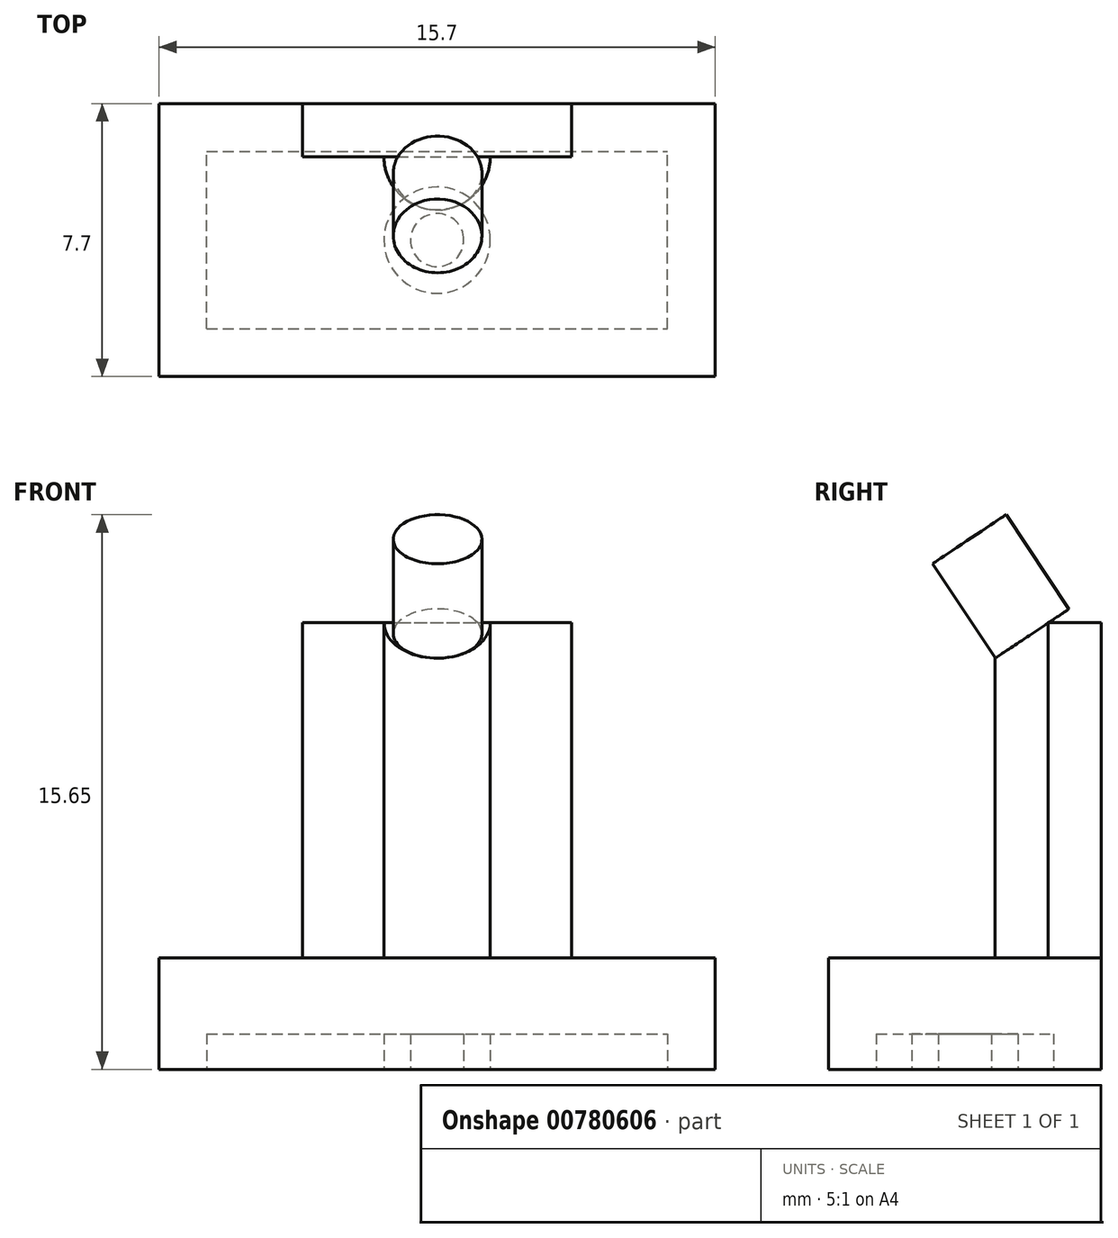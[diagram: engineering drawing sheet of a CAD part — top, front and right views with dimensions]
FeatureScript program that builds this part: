
annotation { "Feature Type Name" : "Feature", "Feature Type Description" : "" }
export const myFeature = defineFeature(function(context is Context, id is Id, definition is map)
    precondition{}
    {
        {
            var Q0;
            Q0=qCreatedBy(makeId("Front.planeOp"),FACE);
            var sketch = newSketch(context, id + "F0", { "sketchPlane" : qUnion([Q0])});
            skLineSegment(sketch, "E0.bottom", {"start": v(0, 0) * mm, "end": v(15.7, 0) * mm});
            skLineSegment(sketch, "E0.top", {"start": v(0, 3.15) * mm, "end": v(15.7, 3.15) * mm});
            skLineSegment(sketch, "E0.left", {"start": v(0, 0) * mm, "end": v(0, 3.15) * mm});
            skLineSegment(sketch, "E0.right", {"start": v(15.7, 0) * mm, "end": v(15.7, 3.15) * mm});
            skLineSegment(sketch, "E1", {"start": v(4.05, 3.15) * mm, "end": v(4.05, 12.6) * mm});
            skLineSegment(sketch, "E2", {"start": v(4.05, 12.6) * mm, "end": v(11.65, 12.6) * mm});
            skLineSegment(sketch, "E3", {"start": v(11.65, 12.6) * mm, "end": v(11.65, 3.15) * mm});
            skSolve(sketch);
        }
        {
            var Q0;
            Q0=makeQuery(id+"F0.imprint","IMPRINT",FACE,{"disambiguationData":[TD([[makeQuery(id+"F0.imprint","IMPRINT",EDGE,{"derivedFrom":sQuery(id+"F0.wireOp",EDGE,"E0.bottom")}),1.0]])]});
            extrude(context, id + "F1", {"entities" : qUnion([Q0]), "depth" : 7.7 * mm, "offsetDistance" : 25 * mm});
        }
        {
            var Q0;
            {var subQ0=sQuery(id+"F0.wireOp",EDGE,"E1");Q0=makeQuery(id+"F0.imprint","IMPRINT",FACE,{"disambiguationData":[TD([[makeQuery(id+"F0.imprint","IMPRINT",EDGE,{"derivedFrom":subQ0}),-1.0]])]});}
            extrude(context, id + "F2", {"entities" : qUnion([Q0]), "operationType" : NewBodyOperationType.ADD, "depth" : 1.5 * mm, "offsetDistance" : 25 * mm});
        }
        {
            var Q0;
            Q0=makeQuery(id+"F1.opExtrude","SWEPT_FACE",FACE,{"disambiguationData":[OSD([sQuery(id+"F0.wireOp",EDGE,"E0.top")])]});
            var sketch = newSketch(context, id + "F3", { "sketchPlane" : qUnion([Q0])});
            skCircle(sketch, "E4", {"center": v(7.85, -1.5) * mm, "radius": 1.5 * mm});
            skSolve(sketch);
        }
        {
            var Q0;
            Q0=qSketchRegion(id+"F3",true);
            extrude(context, id + "F4", {"entities" : qUnion([Q0]), "operationType" : NewBodyOperationType.ADD, "depth" : 9.45 * mm, "offsetDistance" : 25 * mm});
        }
        {
            var Q0;
            Q0=makeQuery(id+"F1.opExtrude","SWEPT_FACE",FACE,{"disambiguationData":[OSD([sQuery(id+"F0.wireOp",EDGE,"E0.bottom")])]});
            var sketch = newSketch(context, id + "F5", { "sketchPlane" : qUnion([Q0])});
            skLineSegment(sketch, "E5.0", {"start": v(1.35, 6.35) * mm, "end": v(14.35, 6.35) * mm});
            skLineSegment(sketch, "E5.1", {"start": v(1.35, 6.35) * mm, "end": v(1.35, 1.35) * mm});
            skLineSegment(sketch, "E5.2", {"start": v(1.35, 1.35) * mm, "end": v(14.35, 1.35) * mm});
            skLineSegment(sketch, "E5.3", {"start": v(14.35, 6.35) * mm, "end": v(14.35, 1.35) * mm});
            skCircle(sketch, "E6", {"center": v(7.85, 3.85) * mm, "radius": 1.5 * mm});
            skPoint(sketch, "E6.centerSnap0", {"position": v(1.35, 3.85) * mm});
            skPoint(sketch, "E6.centerSnap1", {"position": v(7.85, 6.35) * mm});
            skCircle(sketch, "E7", {"center": v(7.85, 3.85) * mm, "radius": 0.75 * mm});
            skSolve(sketch);
        }
        {
            var Q0;
            Q0=makeQuery(id+"F5.imprint","IMPRINT",FACE,{"disambiguationData":[TD([[makeQuery(id+"F5.imprint","IMPRINT",EDGE,{"derivedFrom":sQuery(id+"F5.wireOp",EDGE,"E5.0")}),-1.0]])]});
            var Q1;
            Q1=makeQuery(id+"F5.imprint","IMPRINT",FACE,{"disambiguationData":[TD([[makeQuery(id+"F5.imprint","IMPRINT",EDGE,{"derivedFrom":sQuery(id+"F5.wireOp",EDGE,"E7")}),1.0]])]});
            extrude(context, id + "F6", {"entities" : qUnion([Q0, Q1]), "operationType" : NewBodyOperationType.REMOVE, "oppositeDirection" : true, "depth" : 1 * mm, "offsetDistance" : 25 * mm});
        }
        {
            var Q0;
            Q0=makeQuery(id+"F2.opExtrude","SWEPT_FACE",FACE,{"disambiguationData":[OSD([sQuery(id+"F0.wireOp",EDGE,"E3")])]});
            var sketch = newSketch(context, id + "F7", { "sketchPlane" : qUnion([Q0])});
            skLineSegment(sketch, "E8", {"start": v(-1.5, 12.6) * mm, "end": v(-3, 12.6) * mm});
            skLineSegment(sketch, "E9", {"start": v(-3, 12.6) * mm, "end": v(-3, 11.6) * mm});
            skLineSegment(sketch, "E10", {"start": v(-3, 11.6) * mm, "end": v(-1.5, 12.6) * mm});
            skSolve(sketch);
        }
        {
            var Q0;
            Q0=qSketchRegion(id+"F7",true);
            extrude(context, id + "F8", {"entities" : qUnion([Q0]), "operationType" : NewBodyOperationType.REMOVE, "oppositeDirection" : true, "depth" : 25 * mm, "offsetDistance" : 25 * mm});
        }
        {
            var Q0;
            Q0=makeQuery(id+"F8.boolean.opBoolean","COPY",FACE,{"derivedFrom":makeQuery(id+"F8.opExtrude","SWEPT_FACE",FACE,{"disambiguationData":[OSD([sQuery(id+"F7.wireOp",EDGE,"E10")])]})});
            var sketch = newSketch(context, id + "F9", { "sketchPlane" : qUnion([Q0])});
            skCircle(sketch, "E11", {"center": v(7.86, 5.2) * mm, "radius": 1.25 * mm});
            skSolve(sketch);
        }
        {
            var Q0;
            Q0=qSketchRegion(id+"F9",true);
            extrude(context, id + "F10", {"entities" : qUnion([Q0]), "operationType" : NewBodyOperationType.ADD, "depth" : 3.2 * mm, "offsetDistance" : 25 * mm});
        }
    });
